SOLIDWORKS PART (.sldprt)
format: sldprt  version: not decoded by parser v0  size: 119,808 bytes
history: native  units: mm
features: plane x3, sketch x3, cut_extrude x2, material x1, revolve x1 (+11 scaffold rows collapsed)
feature tree (21):
  scaffold x11  (default folders/planes/origin — collapsed)
  material  "Matériau <non spécifié>"
  plane  "Plan de face"
  plane  "Plan de dessus"
  plane  "Plan de droite"
  sketch  "Esquisse1"  dims[D1=4.0mm]
  revolve  "Révolution1"  Angle=360deg
  sketch  "Esquisse2"  dims[D1=3.0mm]
  cut_extrude  "Extrusion1"  [1 undecoded]
  sketch  "Esquisse3"  dims[c1.D1=1.6mm c1.D2=1.6mm c1.D3=5.0mm c2.D1=3.5mm]
  cut_extrude  "Extrusion2"  Depth=6mm
decode coverage: 5 of 6 modeling features carry decoded parameters
note: 1 parameter value undecoded
note: suppression state not decoded; provenance and decode notes live in map.json
